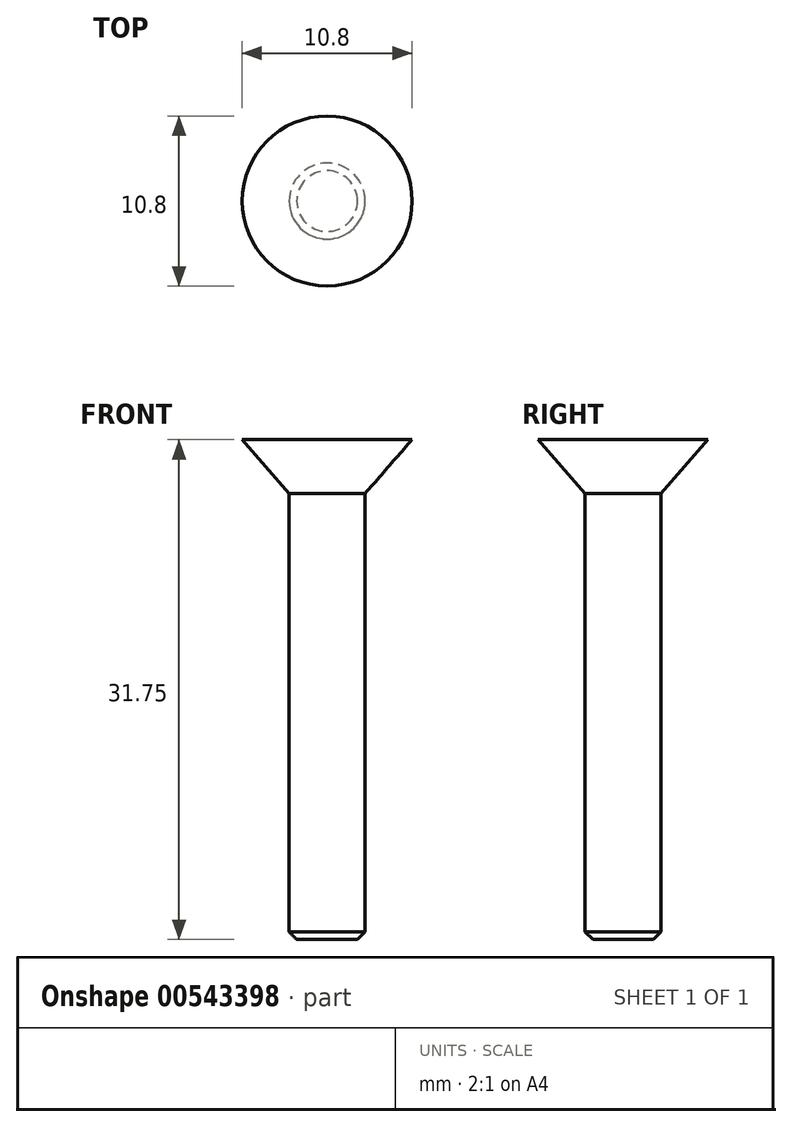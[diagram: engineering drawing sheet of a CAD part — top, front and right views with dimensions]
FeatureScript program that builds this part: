
annotation { "Feature Type Name" : "Feature", "Feature Type Description" : "" }
export const myFeature = defineFeature(function(context is Context, id is Id, definition is map)
    precondition{}
    {
        {
            var Q0;
            Q0=qCreatedBy(makeId("Front.planeOp"),FACE);
            var sketch = newSketch(context, id + "F0", { "sketchPlane" : qUnion([Q0])});
            skLineSegment(sketch, "E0", {"start": v(0, 6.24) * mm, "end": v(0, -9.18) * mm, "construction": true});
            skLineSegment(sketch, "E1", {"start": v(0, 3.43) * mm, "end": v(5.4, 3.43) * mm});
            skLineSegment(sketch, "E2", {"start": v(5.4, 3.43) * mm, "end": v(2.41, 0) * mm});
            skLineSegment(sketch, "E3", {"start": v(2.41, 0) * mm, "end": v(2.41, -28.32) * mm});
            skLineSegment(sketch, "E4", {"start": v(2.41, -28.32) * mm, "end": v(0, -28.32) * mm});
            skLineSegment(sketch, "E5", {"start": v(0, -28.32) * mm, "end": v(0, 3.43) * mm});
            skSolve(sketch);
        }
        {
            var Q0;
            Q0 = qSketchRegion(id + "F0", true);
            var Q1;
            Q1=sQuery(id+"F0.wireOp",EDGE,"E0");
            revolve(context, id + "F1", {"entities" : qUnion([Q0]), "axis" : qUnion([Q1]), "revolveType" : RevolveType.FULL});
        }
        {
            var Q0;
            Q0=makeQuery(id+"F1.opRevolve","SWEPT_EDGE",EDGE,{"disambiguationData":[OSD([sQuery(id+"F0.wireOp",EDGE,"E3"),sQuery(id+"F0.wireOp",EDGE,"E4")])]});
            chamfer(context, id + "F2", {"entities" : qUnion([Q0]), "width" : 0.48 * mm, "tangentPropagation" : true});
        }
    });
